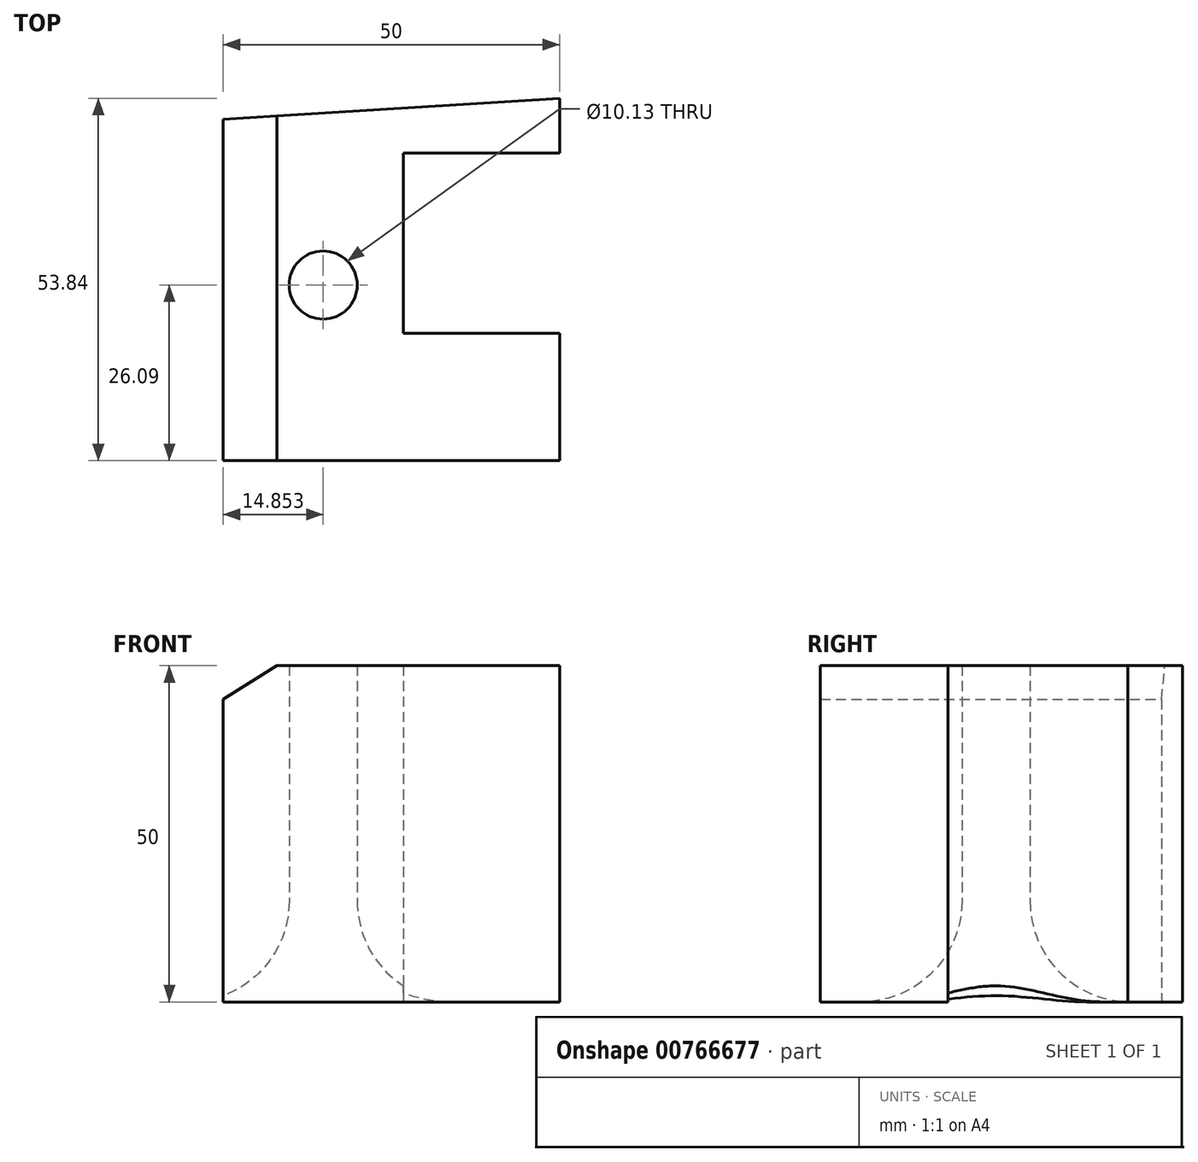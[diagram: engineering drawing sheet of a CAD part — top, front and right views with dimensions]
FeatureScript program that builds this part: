
annotation { "Feature Type Name" : "Feature", "Feature Type Description" : "" }
export const myFeature = defineFeature(function(context is Context, id is Id, definition is map)
    precondition{}
    {
        {
            var Q0;
            Q0=qCreatedBy(makeId("Top.planeOp"),FACE);
            var sketch = newSketch(context, id + "F0", { "sketchPlane" : qUnion([Q0])});
            skLineSegment(sketch, "E0.bottom", {"start": v(-70.2, 39.78) * mm, "end": v(-23.42, 39.78) * mm});
            skLineSegment(sketch, "E0.top", {"start": v(-70.2, 13) * mm, "end": v(-23.42, 13) * mm});
            skLineSegment(sketch, "E0.left", {"start": v(-70.2, 39.78) * mm, "end": v(-70.2, 13) * mm});
            skLineSegment(sketch, "E0.right", {"start": v(-23.42, 39.78) * mm, "end": v(-23.42, 13) * mm});
            skLineSegment(sketch, "E1.bottom", {"start": v(-23.42, 13) * mm, "end": v(-14.14, 13) * mm});
            skLineSegment(sketch, "E1.top", {"start": v(-23.42, 0.5) * mm, "end": v(-14.14, 0.5) * mm});
            skLineSegment(sketch, "E1.left", {"start": v(-23.42, 13) * mm, "end": v(-23.42, 0.5) * mm});
            skLineSegment(sketch, "E1.right", {"start": v(-14.14, 13) * mm, "end": v(-14.14, 0.5) * mm});
            skLineSegment(sketch, "E2.bottom", {"start": v(-47, -5.93) * mm, "end": v(-97, -5.93) * mm});
            skLineSegment(sketch, "E2.top", {"start": v(-47, 49.78) * mm, "end": v(-97, 49.78) * mm});
            skLineSegment(sketch, "E2.left", {"start": v(-47, -5.93) * mm, "end": v(-47, 49.78) * mm});
            skLineSegment(sketch, "E2.right", {"start": v(-97, -5.93) * mm, "end": v(-97, 49.78) * mm});
            skCircle(sketch, "E3", {"center": v(-82.14, 20.16) * mm, "radius": 5.07 * mm});
            skSolve(sketch);
        }
        {
            var Q0;
            {var subQ0=sQuery(id+"F0.wireOp",EDGE,"E0.left");Q0=makeQuery(id+"F0.imprint","IMPRINT",FACE,{"disambiguationData":[TD([[makeQuery(id+"F0.imprint","IMPRINT",EDGE,{"derivedFrom":subQ0}),-1.0]])]});}
            extrude(context, id + "F1", {"entities" : qUnion([Q0]), "depth" : 50 * mm, "offsetDistance" : 25 * mm});
        }
        {
            var Q0;
            Q0=makeQuery(id+"F1.opExtrude","CAP_EDGE",EDGE,{"disambiguationData":[OSD([sQuery(id+"F0.wireOp",EDGE,"E2.right")])],"isStart":false});
            chamfer(context, id + "F2", {"entities" : qUnion([Q0]), "chamferType" : ChamferType.TWO_OFFSETS, "width1" : 5 * mm, "oppositeDirection" : false, "width2" : 8 * mm, "tangentPropagation" : true});
        }
        {
            var Q0;
            Q0=makeQuery(id+"F1.opExtrude","CAP_EDGE",EDGE,{"disambiguationData":[OSD([sQuery(id+"F0.wireOp",EDGE,"E3")])],"isStart":true});
            fillet(context, id + "F3", {"entities" : qUnion([Q0]), "radius" : 15 * mm, "tangentPropagation" : true, "allowEdgeOverflow" : false});
        }
        {
            var Q0;
            Q0=makeQuery(id+"F1.opExtrude","SWEPT_EDGE",EDGE,{"disambiguationData":[OSD([sQuery(id+"F0.wireOp",EDGE,"E2.top"),sQuery(id+"F0.wireOp",EDGE,"E2.right")])]});
            chamfer(context, id + "F4", {"entities" : qUnion([Q0]), "chamferType" : ChamferType.TWO_OFFSETS, "width1" : 5 * mm, "oppositeDirection" : false, "width2" : 80 * mm, "tangentPropagation" : true});
        }
    });
